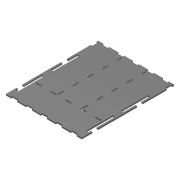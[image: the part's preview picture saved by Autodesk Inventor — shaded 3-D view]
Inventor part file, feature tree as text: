
AUTODESK INVENTOR PART (.ipt)
format: ipt  version: 2020 (Build 240168000, 168)  size: 331,776 bytes
history: native  units: in
note: dims shown in document units (in); Inventor stores cm internally (conversion verified against a paired STEP export)
features: extrude x6, sketch x6
ambient origin geometry x8: Origin, YZ Plane, XZ Plane, XY Plane, X Axis, Y Axis, Z Axis, Center Point
bodies: Solid1 (feature_tree)
feature tree (12):
  extrude  "base"  Depth=12.2047in
  extrude  "Encaixe Laterais"  Depth=0.1969in
  extrude  "Encaixe Divisórias 22cm"  Depth=2.3622in
  extrude  "Extrusion4"  Depth=0.1969in TaperAngle=0.0deg
  extrude  "Extrusion5"  Depth=0.1969in
  extrude  "Extrusion6"  Depth=3.2152in
  sketch  "Sketch1"  dims[d0=10.0394in d1=12.2047in]
  sketch  "Sketch3"  dims[d2=0.1969in d3=0.0in d4=0.1969in]
  sketch  "Sketch4"  dims[d5=0.7874in d6=2.3622in d8=1.9685in d9=0.3937in d11=0.3937in]
  sketch  "Sketch5"  dims[d13=0.7874in d15=9.8425in d16=0.3937in d18=0.3937in d20=0.1969in d21=0.0in]
  sketch  "Sketch6"  dims[d22=9.6457in d23=0.1969in]
  sketch  "Sketch7"  dims[d24=0.7874in d25=3.2152in d26=0.7874in d28=3.2152in d29=1.9685in d31=1.9685in d34=0.1969in d35=0.0in d36=0.7874in d37=0.1969in d38=1.9685in d40=1.9685in d41=0.3937in d43=0.3937in d45=0.689in d46=0.689in d47=0.7874in d49=12.0079in d50=0.3937in d52=0.3937in d54=0.1969in d55=0.0in d56=0.7874in d57=0.1969in d58=1.9685in d60=1.9685in d61=0.3937in d63=0.3937in d65=0.1969in d66=0.0in d67=0.315in d68=3.5433in d69=0.1969in d71=0.315in d72=3.5433in d75=0.1969in d76=0.0in d78=0.1969in d79=1.063in d80=5.7087in]
